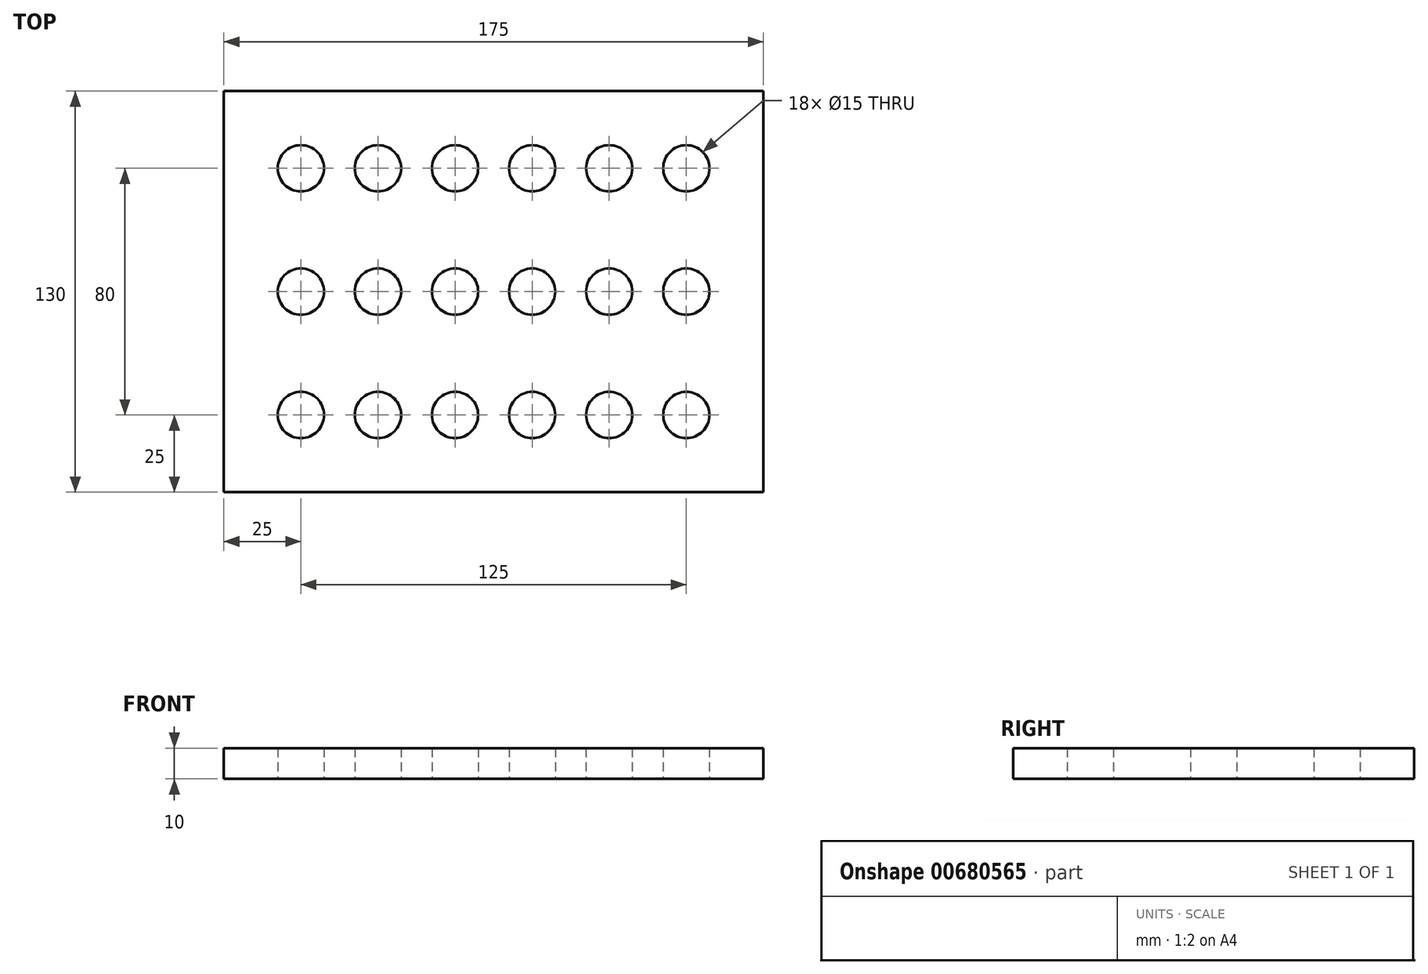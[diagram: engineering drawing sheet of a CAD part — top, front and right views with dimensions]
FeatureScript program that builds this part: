
annotation { "Feature Type Name" : "Feature", "Feature Type Description" : "" }
export const myFeature = defineFeature(function(context is Context, id is Id, definition is map)
    precondition{}
    {
        {
            var Q0;
            Q0=qCreatedBy(makeId("Top.planeOp"),FACE);
            var sketch = newSketch(context, id + "F0", { "sketchPlane" : qUnion([Q0])});
            skLineSegment(sketch, "E0.bottom", {"start": v(-87.5, 65) * mm, "end": v(87.5, 65) * mm});
            skLineSegment(sketch, "E0.top", {"start": v(-87.5, -65) * mm, "end": v(87.5, -65) * mm});
            skLineSegment(sketch, "E0.left", {"start": v(-87.5, 65) * mm, "end": v(-87.5, -65) * mm});
            skLineSegment(sketch, "E0.right", {"start": v(87.5, 65) * mm, "end": v(87.5, -65) * mm});
            skPoint(sketch, "E0.middle", {"position": v(0, 0) * mm});
            skCircle(sketch, "E1", {"center": v(-62.5, 40) * mm, "radius": 7.5 * mm});
            skCircle(sketch, "E2.0.1.0", {"center": v(-62.5, 0) * mm, "radius": 7.5 * mm});
            skCircle(sketch, "E2.0.2.0", {"center": v(-62.5, -40) * mm, "radius": 7.5 * mm});
            skCircle(sketch, "E2.1.0.0", {"center": v(-37.5, 40) * mm, "radius": 7.5 * mm});
            skCircle(sketch, "E2.1.1.0", {"center": v(-37.5, 0) * mm, "radius": 7.5 * mm});
            skCircle(sketch, "E2.1.2.0", {"center": v(-37.5, -40) * mm, "radius": 7.5 * mm});
            skCircle(sketch, "E2.2.0.0", {"center": v(-12.5, 40) * mm, "radius": 7.5 * mm});
            skCircle(sketch, "E2.2.1.0", {"center": v(-12.5, 0) * mm, "radius": 7.5 * mm});
            skCircle(sketch, "E2.2.2.0", {"center": v(-12.5, -40) * mm, "radius": 7.5 * mm});
            skCircle(sketch, "E2.3.0.0", {"center": v(12.5, 40) * mm, "radius": 7.5 * mm});
            skCircle(sketch, "E2.3.1.0", {"center": v(12.5, 0) * mm, "radius": 7.5 * mm});
            skCircle(sketch, "E2.3.2.0", {"center": v(12.5, -40) * mm, "radius": 7.5 * mm});
            skCircle(sketch, "E2.4.0.0", {"center": v(37.5, 40) * mm, "radius": 7.5 * mm});
            skCircle(sketch, "E2.4.1.0", {"center": v(37.5, 0) * mm, "radius": 7.5 * mm});
            skCircle(sketch, "E2.4.2.0", {"center": v(37.5, -40) * mm, "radius": 7.5 * mm});
            skCircle(sketch, "E2.5.0.0", {"center": v(62.5, 40) * mm, "radius": 7.5 * mm});
            skCircle(sketch, "E2.5.1.0", {"center": v(62.5, 0) * mm, "radius": 7.5 * mm});
            skCircle(sketch, "E2.5.2.0", {"center": v(62.5, -40) * mm, "radius": 7.5 * mm});
            skLineSegment(sketch, "E2.direction1", {"start": v(-62.5, 40) * mm, "end": v(-37.5, 40) * mm, "construction": true});
            skLineSegment(sketch, "E2.direction2", {"start": v(-62.5, 40) * mm, "end": v(-62.5, 0) * mm, "construction": true});
            skSolve(sketch);
        }
        {
            var Q0;
            Q0 = qSketchRegion(id + "F0", true);
            extrude(context, id + "F1", {"entities" : qUnion([Q0]), "depth" : 10 * mm, "offsetDistance" : 25 * mm});
        }
    });
